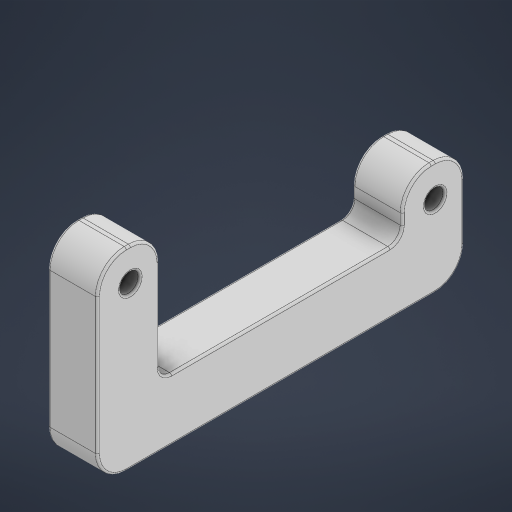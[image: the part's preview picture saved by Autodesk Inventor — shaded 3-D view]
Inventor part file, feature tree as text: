
AUTODESK INVENTOR PART (.ipt)
format: ipt  version: 2024.2 (Build 282272000, 272)  size: 268,800 bytes
history: native  units: mm
features: fillet x2, extrude x1, sketch x1
ambient origin geometry x8: Origin, YZ Plane, XZ Plane, XY Plane, X Axis, Y Axis, Z Axis, Center Point
bodies: Solid1 (feature_tree)
feature tree (4):
  extrude  "Extrusion1"  Depth=0.5mm
  fillet  "Fillet1"  Radius=4.75mm
  fillet  "Fillet2"  Radius=59.0mm
  sketch  "Sketch1"  dims[d0=76.5mm d1=4.75mm d2=4.75mm d3=59.0mm d4=7.0mm d5=8.0mm d6=15.0mm d7=15.0mm d9=8.0mm d10=8.0mm d11=24.0mm d12=15.0mm d13=3.0mm d14=7.0mm d15=12.0mm d16=0.0mm d17=0.5mm d18=0.5mm]
